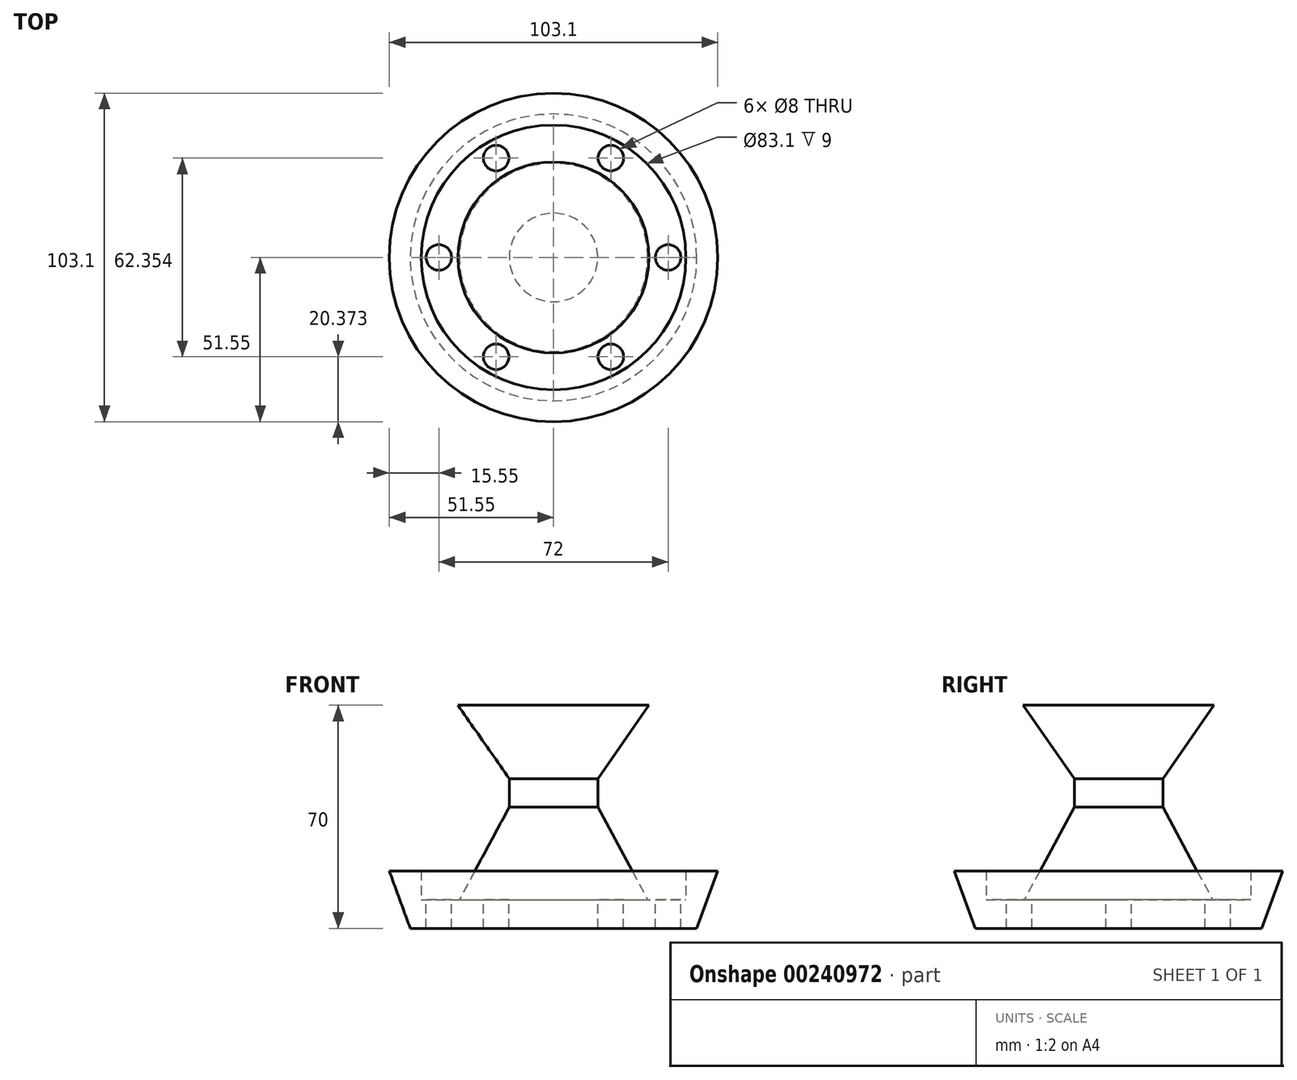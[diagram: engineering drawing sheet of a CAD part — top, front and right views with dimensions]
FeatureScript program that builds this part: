
annotation { "Feature Type Name" : "Feature", "Feature Type Description" : "" }
export const myFeature = defineFeature(function(context is Context, id is Id, definition is map)
    precondition{}
    {
        {
            var Q0;
            Q0=qCreatedBy(makeId("Front.planeOp"),FACE);
            var sketch = newSketch(context, id + "F0", { "sketchPlane" : qUnion([Q0])});
            skLineSegment(sketch, "E0", {"start": v(0, 70) * mm, "end": v(-30, 70) * mm});
            skLineSegment(sketch, "E1", {"start": v(-30, 70) * mm, "end": v(-13.9, 47) * mm});
            skLineSegment(sketch, "E2", {"start": v(-13.9, 47) * mm, "end": v(-13.9, 38) * mm});
            skLineSegment(sketch, "E3", {"start": v(-13.9, 38) * mm, "end": v(-29.55, 9) * mm});
            skLineSegment(sketch, "E4", {"start": v(-29.55, 9) * mm, "end": v(-41.55, 9) * mm});
            skLineSegment(sketch, "E5", {"start": v(-41.55, 9) * mm, "end": v(-41.55, 18) * mm});
            skLineSegment(sketch, "E6", {"start": v(-41.55, 18) * mm, "end": v(-51.55, 18) * mm});
            skLineSegment(sketch, "E7", {"start": v(-51.55, 18) * mm, "end": v(-45, 0) * mm});
            skLineSegment(sketch, "E8", {"start": v(-45, 0) * mm, "end": v(0, 0) * mm});
            skLineSegment(sketch, "E9", {"start": v(0, 0) * mm, "end": v(0, 70) * mm});
            skSolve(sketch);
        }
        {
            var Q0;
            Q0 = qSketchRegion(id + "F0", true);
            var Q1;
            Q1=sQuery(id+"F0.wireOp",EDGE,"E9");
            revolve(context, id + "F1", {"entities" : qUnion([Q0]), "axis" : qUnion([Q1]), "revolveType" : RevolveType.FULL});
        }
        {
            var Q0;
            Q0=makeQuery(id+"F1.opRevolve","SWEPT_FACE",FACE,{"disambiguationData":[OSD([sQuery(id+"F0.wireOp",EDGE,"E4")])]});
            var sketch = newSketch(context, id + "F2", { "sketchPlane" : qUnion([Q0])});
            skCircle(sketch, "E10", {"center": v(-36, 0) * mm, "radius": 4 * mm});
            skCircle(sketch, "E11.1.0", {"center": v(-18, -31.18) * mm, "radius": 4 * mm});
            skCircle(sketch, "E11.2.0", {"center": v(18, -31.18) * mm, "radius": 4 * mm});
            skCircle(sketch, "E11.3.0", {"center": v(36, 0) * mm, "radius": 4 * mm});
            skCircle(sketch, "E11.4.0", {"center": v(18, 31.18) * mm, "radius": 4 * mm});
            skCircle(sketch, "E11.5.0", {"center": v(-18, 31.18) * mm, "radius": 4 * mm});
            skPoint(sketch, "E11.center", {"position": v(0, 0) * mm});
            skSolve(sketch);
        }
        {
            var Q0;
            Q0 = qSketchRegion(id + "F2", true);
            extrude(context, id + "F3", {"entities" : qUnion([Q0]), "operationType" : NewBodyOperationType.REMOVE, "oppositeDirection" : true, "depth" : 25 * mm});
        }
    });
